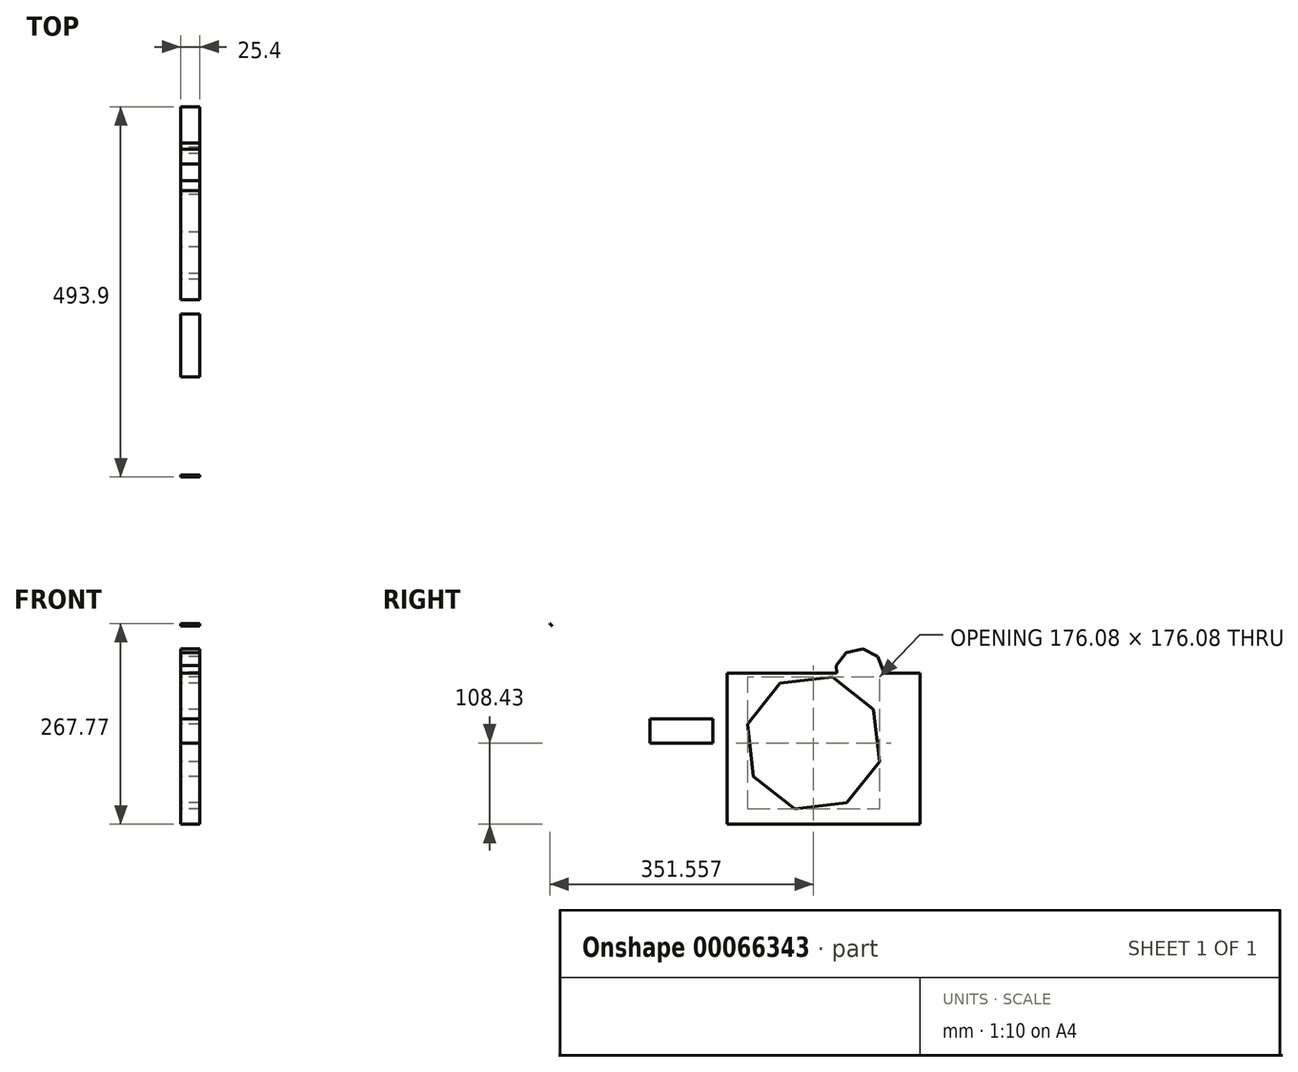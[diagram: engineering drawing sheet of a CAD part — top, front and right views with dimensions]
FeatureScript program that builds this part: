
annotation { "Feature Type Name" : "Feature", "Feature Type Description" : "" }
export const myFeature = defineFeature(function(context is Context, id is Id, definition is map)
    precondition{}
    {
        {
            var Q0;
            Q0=qCreatedBy(makeId("Right.planeOp"),FACE);
            var sketch = newSketch(context, id + "F0", { "sketchPlane" : qUnion([Q0])});
            skLineSegment(sketch, "E0.bottom", {"start": v(-98.97, 93.1) * mm, "end": v(158.18, 93.1) * mm});
            skLineSegment(sketch, "E0.top", {"start": v(-98.97, -108.43) * mm, "end": v(158.18, -108.43) * mm});
            skLineSegment(sketch, "E0.left", {"start": v(-98.97, 93.1) * mm, "end": v(-98.97, -108.43) * mm});
            skLineSegment(sketch, "E0.right", {"start": v(158.18, 93.1) * mm, "end": v(158.18, -108.43) * mm});
            skLineSegment(sketch, "E1.bottom", {"start": v(-118.42, 108.95) * mm, "end": v(-181.16, 108.95) * mm});
            skLineSegment(sketch, "E1.top", {"start": v(-118.42, 148.49) * mm, "end": v(-181.16, 148.49) * mm});
            skLineSegment(sketch, "E1.left", {"start": v(-118.42, 108.95) * mm, "end": v(-118.42, 148.49) * mm});
            skLineSegment(sketch, "E1.right", {"start": v(-181.16, 108.95) * mm, "end": v(-181.16, 148.49) * mm});
            skLineSegment(sketch, "E2.bottom", {"start": v(-118.42, 0) * mm, "end": v(-202.37, 0) * mm});
            skLineSegment(sketch, "E2.top", {"start": v(-118.42, 32.05) * mm, "end": v(-202.37, 32.05) * mm});
            skLineSegment(sketch, "E2.left", {"start": v(-118.42, 0) * mm, "end": v(-118.42, 32.05) * mm});
            skLineSegment(sketch, "E2.right", {"start": v(-202.37, 0) * mm, "end": v(-202.37, 32.05) * mm});
            skCircle(sketch, "E3", {"center": v(-302.22, 184.02) * mm, "radius": 41.6 * mm});
            skFitSpline(sketch, "E4", {"points": [v(-309.5, 224.98) * mm, v(-411.87, 267.42) * mm, v(-397.73, 211.88) * mm, v(-392.43, 150.55) * mm, v(-354.43, 131.04) * mm, v(-335.72, 159.34) * mm, v(-332.8, 155.8) * mm, v(-332.8, 155.8) * mm], "startDerivative": vector(-547.23, 301.43) * mm, "endDerivative": vector(0.05, 0) * mm});
            skFitSpline(sketch, "E5", {"points": [v(-302.22, 184.02) * mm, v(-244.85, 140.54) * mm, v(-243.97, 136.53) * mm], "startDerivative": vector(97.91, -67.21) * mm, "endDerivative": vector(-1.83, -17.62) * mm});
            skCircle(sketch, "E6.cCircle", {"center": v(15.84, 0) * mm, "radius": 84.57 * mm, "construction": true});
            skLineSegment(sketch, "E6.0", {"start": v(103.88, -25.08) * mm, "end": v(60.35, -79.99) * mm});
            skLineSegment(sketch, "E6.1", {"start": v(60.35, -79.99) * mm, "end": v(-9.25, -88.04) * mm});
            skLineSegment(sketch, "E6.2", {"start": v(-9.25, -88.04) * mm, "end": v(-64.15, -44.52) * mm});
            skLineSegment(sketch, "E6.3", {"start": v(-64.15, -44.52) * mm, "end": v(-72.2, 25.08) * mm});
            skLineSegment(sketch, "E6.4", {"start": v(-72.2, 25.08) * mm, "end": v(-28.68, 79.99) * mm});
            skLineSegment(sketch, "E6.5", {"start": v(-28.68, 79.99) * mm, "end": v(40.92, 88.04) * mm});
            skLineSegment(sketch, "E6.6", {"start": v(40.92, 88.04) * mm, "end": v(95.83, 44.52) * mm});
            skLineSegment(sketch, "E6.7", {"start": v(95.83, 44.52) * mm, "end": v(103.88, -25.08) * mm});
            skPoint(sketch, "E6.0.midPoint", {"position": v(82.11, -52.54) * mm});
            skCircle(sketch, "E7.cCircle", {"center": v(77.15, 93.1) * mm, "radius": 30.6 * mm, "construction": true});
            skLineSegment(sketch, "E7.0", {"start": v(81.57, 125.37) * mm, "end": v(101.27, 114.98) * mm});
            skLineSegment(sketch, "E7.1", {"start": v(101.27, 114.98) * mm, "end": v(109.68, 94.36) * mm});
            skLineSegment(sketch, "E7.2", {"start": v(109.68, 94.36) * mm, "end": v(102.87, 73.15) * mm});
            skLineSegment(sketch, "E7.3", {"start": v(102.87, 73.15) * mm, "end": v(84.03, 61.28) * mm});
            skLineSegment(sketch, "E7.4", {"start": v(84.03, 61.28) * mm, "end": v(61.96, 64.31) * mm});
            skLineSegment(sketch, "E7.5", {"start": v(61.96, 64.31) * mm, "end": v(47, 80.81) * mm});
            skLineSegment(sketch, "E7.6", {"start": v(47, 80.81) * mm, "end": v(46.15, 103.07) * mm});
            skLineSegment(sketch, "E7.7", {"start": v(46.15, 103.07) * mm, "end": v(59.8, 120.66) * mm});
            skLineSegment(sketch, "E7.8", {"start": v(59.8, 120.66) * mm, "end": v(81.57, 125.37) * mm});
            skPoint(sketch, "E7.0.midPoint", {"position": v(91.42, 120.17) * mm});
            skSolve(sketch);
        }
        {
            var Q0;
            Q0=makeQuery(id+"F0.imprint","IMPRINT",FACE,{"disambiguationData":[TD([[makeQuery(id+"F0.imprint","IMPRINT",EDGE,{"derivedFrom":sQuery(id+"F0.wireOp",EDGE,"E2.bottom")}),-1.0]])]});
            var Q1;
            Q1=makeQuery(id+"F0.imprint","IMPRINT",FACE,{"disambiguationData":[TD([[makeQuery(id+"F0.imprint","IMPRINT",EDGE,{"derivedFrom":sQuery(id+"F0.wireOp",EDGE,"E7.0")}),-1.0]])]});
            var Q2;
            {var subQ0=sQuery(id+"F0.wireOp",EDGE,"E4");var subQ1=sQuery(id+"F0.wireOp",EDGE,"E3");var subQ2=makeQuery(id+"F0.imprint","INTERSECT",VERTEX,{"disambiguationData":[OD(1.0)],"derivedFrom":[subQ1,subQ0]});Q2=makeQuery(id+"F0.imprint","IMPRINT",FACE,{"disambiguationData":[TD([[makeQuery(id+"F0.imprint","IMPRINT",EDGE,{"disambiguationData":[TD([[subQ2,1.0]])],"derivedFrom":subQ1}),1.0]])]});}
            var Q3;
            Q3=makeQuery(id+"F0.imprint","IMPRINT",FACE,{"disambiguationData":[TD([[makeQuery(id+"F0.imprint","IMPRINT",EDGE,{"derivedFrom":sQuery(id+"F0.wireOp",EDGE,"E0.top")}),1.0]])]});
            var Q4;
            {var subQ1=sQuery(id+"F0.wireOp",EDGE,"E3");var subQ5=makeQuery(id+"F0.imprint","IMPRINT",VERTEX,{"derivedFrom":subQ1});Q4=makeQuery(id+"F0.imprint","IMPRINT",FACE,{"disambiguationData":[TD([[makeQuery(id+"F0.imprint","IMPRINT",EDGE,{"disambiguationData":[TD([[subQ5,1.0]])],"derivedFrom":subQ1}),1.0]])]});}
            var Q5;
            {var subQ0=sQuery(id+"F0.wireOp",EDGE,"E7.3");Q5=makeQuery(id+"F0.imprint","IMPRINT",FACE,{"disambiguationData":[TD([[makeQuery(id+"F0.imprint","IMPRINT",EDGE,{"derivedFrom":subQ0}),-1.0]])]});}
            extrude(context, id + "F1", {"entities" : qUnion([Q0, Q1, Q2, Q3, Q4, Q5]), "depth" : 25.4 * mm});
        }
    });
